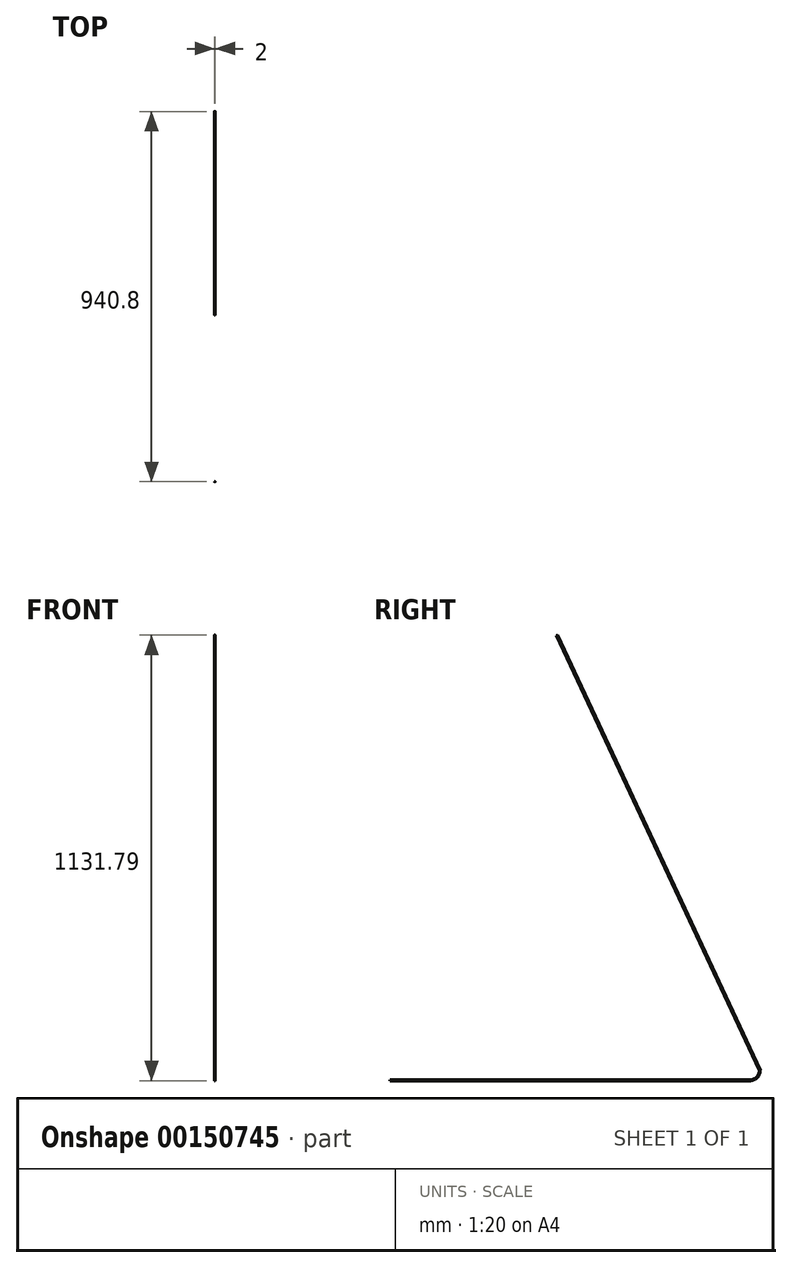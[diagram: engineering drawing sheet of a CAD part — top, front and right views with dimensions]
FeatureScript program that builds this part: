
annotation { "Feature Type Name" : "Feature", "Feature Type Description" : "" }
export const myFeature = defineFeature(function(context is Context, id is Id, definition is map)
    precondition{}
    {
        {
            var Q0;
            Q0=qCreatedBy(makeId("Front.planeOp"),FACE);
            var sketch = newSketch(context, id + "F0", { "sketchPlane" : qUnion([Q0])});
            skCircle(sketch, "E0", {"center": v(0, 0) * mm, "radius": 1 * mm});
            skSolve(sketch);
        }
        {
            var Q0;
            Q0=qCreatedBy(makeId("Right.planeOp"),FACE);
            var sketch = newSketch(context, id + "F1", { "sketchPlane" : qUnion([Q0])});
            skLineSegment(sketch, "E1", {"start": v(0, 0) * mm, "end": v(914.4, 0) * mm});
            skArc(sketch, "E2", {"start": v(914.4, 0) * mm, "mid": v(932.36, 7.44) * mm, "end": v(939.8, 25.4) * mm});
            skLineSegment(sketch, "E3", {"start": v(939.8, 25.4) * mm, "end": v(424.54, 1130.37) * mm});
            skSolve(sketch);
        }
        {
            var Q0;
            Q0=makeQuery(id+"F0.imprint","IMPRINT",FACE,{"disambiguationData":[TD([[makeQuery(id+"F0.imprint","IMPRINT",EDGE,{"derivedFrom":sQuery(id+"F0.wireOp",EDGE,"E0")}),1.0]])]});
            var Q1;
            Q1=sQuery(id+"F1.wireOp",EDGE,"E1");
            var Q2;
            Q2=sQuery(id+"F1.wireOp",EDGE,"E2");
            var Q3;
            Q3=sQuery(id+"F1.wireOp",EDGE,"E3");
            sweep(context, id + "F2", {"profiles" : qUnion([Q0]), "path" : qUnion([Q1, Q2, Q3])});
        }
    });
